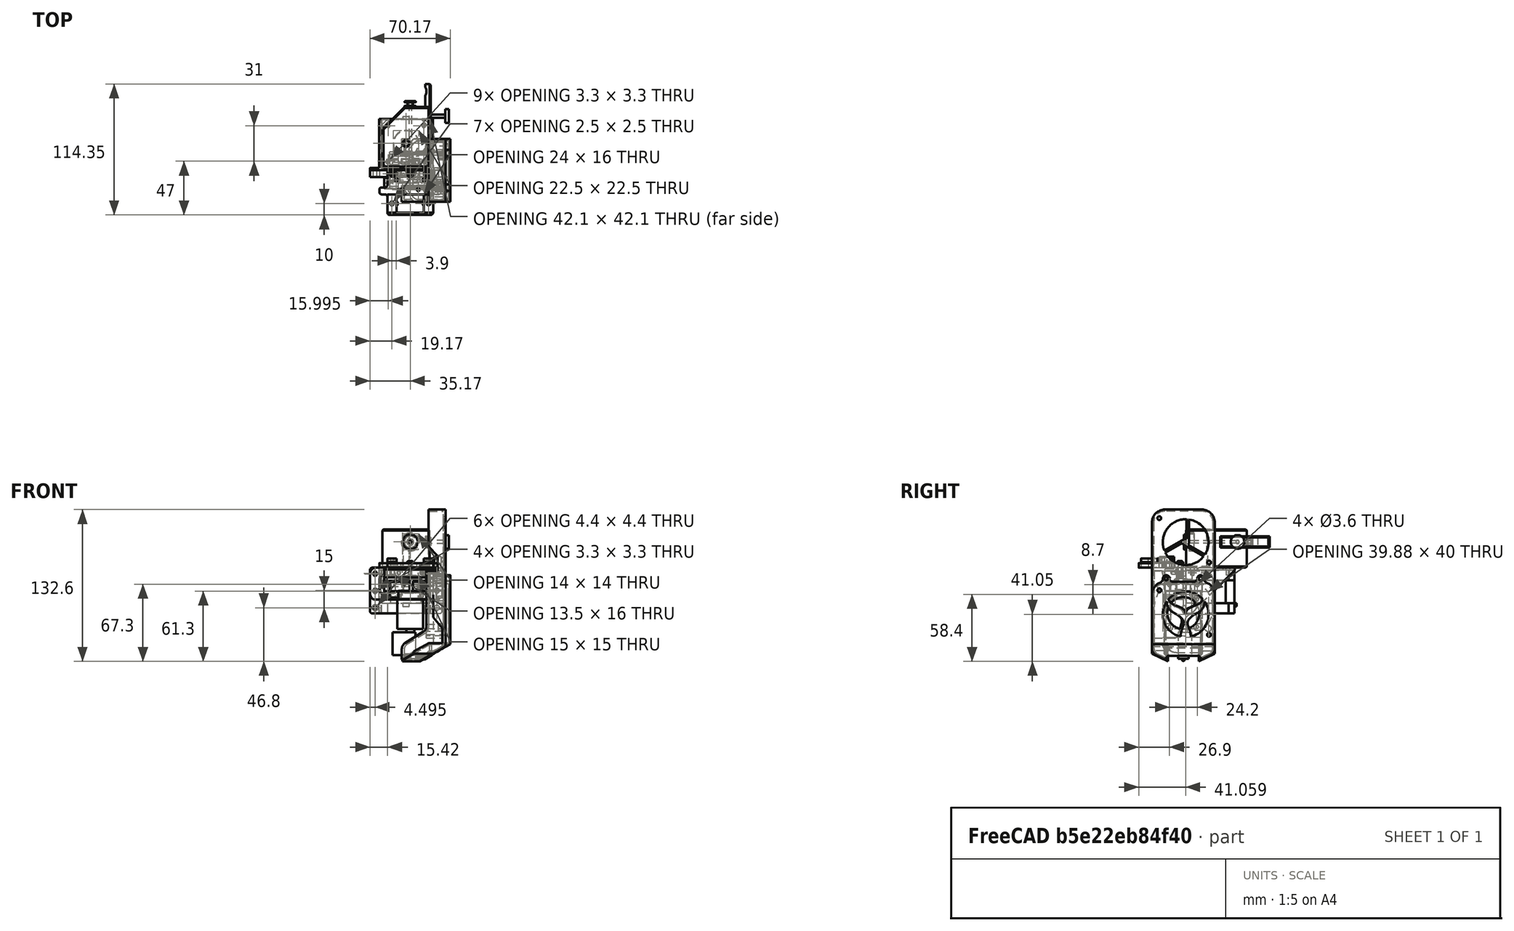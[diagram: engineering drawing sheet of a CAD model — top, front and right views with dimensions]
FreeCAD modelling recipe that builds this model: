
FCSTD DOCUMENT  (FreeCAD 0.21R33675 (Git))
Label: V6火山+5015方案B
License: All rights reserved
LicenseURL: http://en.wikipedia.org/wiki/All_rights_reserved
objects: Sketcher::SketchObject×31, PartDesign::Pad×16, PartDesign::Pocket×15, Part::Feature×13, PartDesign::Body×6, PartDesign::Fillet×4, PartDesign::Chamfer×4, PartDesign::Thickness×2, Part::Fuse×2, PartDesign::Revolution×1, App::Part×1, PartDesign::Mirrored×1, Part::Mirroring×1
note: 138 computed .brp shape members not serialized (recipe doc carries the construction recipe); baked Part::Feature solids carry a one-line shape summary decoded from their .brp

FEATURE [Sketcher::SketchObject] Sketch015
  FullyConstrained = true
  MapMode = 5
  Placement = pos=(0,0,0) rot=(0.57735,0.57735,0.57735;2.0944rad)
  Support = -> [YZ_Plane002]
  sketch-geometry (17):
    g0: LineSegment StartX=0 StartY=4 StartZ=0 EndX=8 EndY=4 EndZ=0
    g1: LineSegment StartX=8 StartY=4 StartZ=0 EndX=8 EndY=0 EndZ=0
    g2: LineSegment StartX=8 StartY=0 StartZ=0 EndX=6 EndY=0 EndZ=0
    g3: LineSegment StartX=6 StartY=0 StartZ=0 EndX=6 EndY=-6 EndZ=0
    g4: LineSegment StartX=6 StartY=-6 StartZ=0 EndX=8 EndY=-6 EndZ=0
    g5: LineSegment StartX=8 StartY=-6 StartZ=0 EndX=8 EndY=-12.5 EndZ=0
    g6: LineSegment StartX=8 StartY=-12.5 StartZ=0 EndX=11.15 EndY=-12.5 EndZ=0
    g7: LineSegment StartX=11.15 StartY=-12.5 StartZ=0 EndX=11.15 EndY=-39 EndZ=0
    g8: LineSegment StartX=11.15 StartY=-39 StartZ=0 EndX=3.5 EndY=-39 EndZ=0
    g9: LineSegment StartX=0.5 StartY=-67 StartZ=0 EndX=0 EndY=-67 EndZ=0
    g10: LineSegment StartX=3.5 StartY=-39 StartZ=0 EndX=3.5 EndY=-62 EndZ=0
    g11: LineSegment StartX=0 StartY=4 StartZ=0 EndX=0 EndY=-67 EndZ=0
    g12: GeomPoint X=3.5 Y=-42 Z=0
    g13: LineSegment StartX=3.5 StartY=-62 StartZ=0 EndX=4.5 EndY=-62 EndZ=0
    g14: LineSegment StartX=4.5 StartY=-62 StartZ=0 EndX=4.5 EndY=-65 EndZ=0
    g15: LineSegment StartX=4.5 StartY=-65 StartZ=0 EndX=1.90042 EndY=-65 EndZ=0
    g16: LineSegment StartX=1.90042 StartY=-65 StartZ=0 EndX=0.5 EndY=-67 EndZ=0
  constraints (50):
    c: PointOnObject(g0,g-2)
    c: Horizontal(g0)
    c: Coincident(g1,g0)
    c: Vertical(g1)
    c: Coincident(g2,g1)
    c: Coincident(g3,g2)
    c: Coincident(g4,g3)
    c: Horizontal(g4)
    c: Horizontal(g2)
    c: Distance(g0) = 8
    c: Distance(g1) = 4
    c: Distance(g3) = 6
    c: Distance(g2) = 2
    c: Distance(g4) = 2
    c: Coincident(g5,g4)
    c: Horizontal(g6)
    c: Coincident(g7,g6)
    c: Vertical(g7)
    c: Vertical(g5)
    c: Coincident(g6,g5)
    c: DistanceX(g-2,g6) = 11.15
    c: Coincident(g8,g7)
    c: Horizontal(g8)
    c: DistanceX(g-2,g8) = 3.5
    c: DistanceY(g7,g0) = 43
    c: Distance(g5) = 6.5
    c: PointOnObject(g9,g-2)
    c: Horizontal(g9)
    c: Distance(g9) = 0.5
    c: Coincident(g10,g8)
    c: Vertical(g10)
    c: Coincident(g11,g0)
    c: Coincident(g11,g9)
    c: Vertical(g3)
    c: PointOnObject(g2,g-1)
    c: PointOnObject(g12,g10)
    c: Distance(g12,g8) = 3
    c: Distance(g12,g10) = 20
    c: Coincident(g10,g13)
    c: Horizontal(g13)
    c: Coincident(g13,g14)
    c: Vertical(g14)
    c: Coincident(g14,g15)
    c: Horizontal(g15)
    c: Coincident(g15,g16)
    c: Coincident(g16,g9)
    c: Angle(g16,g15) = 2.18166
    c: Distance(g13) = 1
    c: DistanceY(g9,g13) = 5
    c: Distance(g14) = 3
FEATURE [PartDesign::Revolution] Revolution
  Angle = 360
  Axis = (-2e-16,3e-16,1)
  Base = (0,0,0)
  Placement = pos=(0,0,0) rot=(0.57735,0.57735,0.57735;2.0944rad)
  Profile = -> Sketch015
  ReferenceAxis = -> Sketch015 [V_Axis]
  Reversed = true
FEATURE [Sketcher::SketchObject] Sketch016
  ExternalGeometry = -> [Revolution]
  FullyConstrained = true
  MapMode = 5
  Placement = pos=(0,0,0) rot=(1,0,0;1.5708rad)
  Support = -> [XZ_Plane002]
  sketch-geometry (6):
    g0: LineSegment StartX=-3.5 StartY=-62 StartZ=0 EndX=-15.5 EndY=-62 EndZ=0
    g1: LineSegment StartX=-15.5 StartY=-62 StartZ=0 EndX=-15.5 EndY=-42 EndZ=0
    g2: LineSegment StartX=-15.5 StartY=-42 StartZ=0 EndX=4.5 EndY=-42 EndZ=0
    g3: LineSegment StartX=4.5 StartY=-42 StartZ=0 EndX=4.5 EndY=-62 EndZ=0
    g4: LineSegment StartX=4.5 StartY=-62 StartZ=0 EndX=3.5 EndY=-62 EndZ=0
    g5: LineSegment StartX=-3.5 StartY=-62 StartZ=0 EndX=3.5 EndY=-62 EndZ=0
  constraints (16):
    c: Coincident(g0,g-3)
    c: Horizontal(g0)
    c: Coincident(g1,g0)
    c: Vertical(g1)
    c: Coincident(g2,g1)
    c: Horizontal(g2)
    c: Coincident(g3,g2)
    c: Vertical(g3)
    c: Coincident(g4,g3)
    c: Coincident(g4,g-3)
    c: Horizontal(g4)
    c: Distance(g3) = 20
    c: Distance(g1,g2) = 20
    c: DistanceX(g-2,g0) = -15.5
    c: Coincident(g5,g0)
    c: Coincident(g5,g4)
FEATURE [PartDesign::Pad] Pad006  label="薄"
  BaseFeature = -> Revolution
  Direction = (0,-1,-2e-16)
  Length = 4.5
  Length2 = 10
  Placement = pos=(0,0,0) rot=(0.57735,0.57735,0.57735;2.0944rad)
  Profile = -> Sketch016
  ReferenceAxis = -> Sketch016 [N_Axis]
  Type = 0
FEATURE [PartDesign::Pad] Pad007  label="厚"
  BaseFeature = -> Pad006
  Direction = (0,-1,-2e-16)
  Length = 7
  Length2 = 10
  Placement = pos=(0,0,0) rot=(0.57735,0.57735,0.57735;2.0944rad)
  Profile = -> Sketch016
  ReferenceAxis = -> Sketch016 [N_Axis]
  Reversed = true
  Type = 0
FEATURE [PartDesign::Body] Body002  label="E3DV6火山（玻璃热敏）"
  Group = -> [Sketch015,Revolution,Sketch016,Pad006,Pad007]
  Origin = -> Origin002
  Tip = -> Pad007
FEATURE [Part::Feature] Part__Feature166  label="<unrecoverable-encoding: 13 bytes cea2d18dd09ecebbbfaab9d6... md5=9adbc4b6>A125V003"
  Placement = pos=(23.9,-14.5,21.31) rot=(0,0,-1;1.5708rad)
  shape: bbox 13.5 x 14.59 x 5.62 mm, 42 faces (baked)
FEATURE [Part::Feature] Part__Feature167  label="MGN12H»¬¿002"
  Placement = pos=(0,-19,0) rot=(0,-1,0;1.5708rad)
  shape: bbox 45.4 x 10 x 27 mm, 34 faces (baked)
FEATURE [Part::Feature] Part__Feature169  label="ɢɈ¹ܰ²װ°"
  Placement = pos=(0,-19.5,16.5) rot=(0,0,1;0rad)
  shape: bbox 54 x 39 x 4 mm, 68 faces (baked)
FEATURE [Part::Feature] Part__Feature172  label="同步带压片"
  Placement = pos=(-16,-29,21) rot=(0,0,1;0rad)
  shape: bbox 8 x 16 x 3 mm, 12 faces (baked)
FEATURE [Part::Feature] Part__Feature173  label="同步带压片001"
  Placement = pos=(16,-29,21) rot=(0,1,0;3.14159rad)
  shape: bbox 8 x 16 x 3 mm, 12 faces (baked)
FEATURE [Part::Feature] Part__Feature174  label="42步进电机004"
  Placement = pos=(-3.675,23.5,12.5) rot=(0,0,1;0rad)
  shape: bbox 42.3 x 44.3 x 62 mm, 50 faces (baked)
FEATURE [Part::Feature] Part__Feature175  label="42步进电机支架"
  Placement = pos=(-3.675,23.5,14.5) rot=(0,0,1;0rad)
  shape: bbox 63 x 45 x 40 mm, 42 faces (baked)
FEATURE [Part::Feature] Part__Feature176  label="MGN12H滑筷棯接颁灅住"
  Placement = pos=(0,0,0) rot=(0.57735,-0.57735,-0.57735;2.0944rad)
  shape: bbox 63 x 6 x 28 mm, 64 faces (baked)
FEATURE [Part::Feature] Part__Feature177  label="BMG挤出机"
  Placement = pos=(0,2.35,37) rot=(0,0,1;0rad)
  shape: bbox 58 x 75 x 33.5 mm, 84 faces (baked)
FEATURE [Part::Feature] Part__Feature179  label="内六角平圆头螺钉M3¡Á029"
  Placement = pos=(0,-3,18.5) rot=(1,0,0;1.5708rad)
  shape: bbox 6.17 x 6.17 x 12.2 mm, 24 faces (baked)
FEATURE [Part::Feature] Part__Feature180  label="内六角平圆头螺钉M3¡Á030"
  Placement = pos=(15,-3,18.5) rot=(1,0,0;1.5708rad)
  shape: bbox 6.17 x 6.17 x 12.2 mm, 24 faces (baked)
FEATURE [Part::Feature] Part__Feature178  label="内六角平圆头螺钉M3¡Á028"
  Placement = pos=(-15,-3,18.5) rot=(1,0,0;1.5708rad)
  shape: bbox 6.17 x 6.17 x 12.2 mm, 24 faces (baked)
FEATURE [App::Part] CR10________________________1  label="CR10近程喷嘴模块1"
  Group = -> [Part__Feature166,Part__Feature167,Part__Feature169,Part__Feature172,Part__Feature173,Part__Feature174,Part__Feature175,Part__Feature176,Part__Feature177,Part__Feature178,Part__Feature179,Part__Feature180]
  Origin = -> Origin006
  Placement = pos=(-36.5,0,8.1) rot=(0.57735,0.57735,0.57735;2.0944rad)
FEATURE [Sketcher::SketchObject] Sketch017
  FullyConstrained = true
  MapMode = 5
  Placement = pos=(0,0,0) rot=(0.57735,0.57735,0.57735;2.0944rad)
  Support = -> [YZ_Plane007]
  sketch-geometry (18):
    g0: LineSegment StartX=-16 StartY=2.25 StartZ=0 EndX=-16 EndY=0 EndZ=0
    g1: LineSegment StartX=-16 StartY=0 StartZ=0 EndX=-16 EndY=-5.8 EndZ=0
    g2: LineSegment StartX=-16 StartY=-5.8 StartZ=0 EndX=-16 EndY=-11.8 EndZ=0
    g3: LineSegment StartX=-16 StartY=-11.8 StartZ=0 EndX=16 EndY=-11.8 EndZ=0
    g4: LineSegment StartX=16 StartY=-11.8 StartZ=0 EndX=16 EndY=-5.8 EndZ=0
    g5: LineSegment StartX=16 StartY=-5.8 StartZ=0 EndX=16 EndY=0 EndZ=0
    g6: LineSegment StartX=16 StartY=0 StartZ=0 EndX=16 EndY=2.25 EndZ=0
    g7: Circle CenterX=-7 CenterY=-8.9 CenterZ=0 NormalX=0 NormalY=0 NormalZ=1 AngleXU=0 Radius=1.8
    g8: Circle CenterX=7 CenterY=-8.9 CenterZ=0 NormalX=0 NormalY=0 NormalZ=1 AngleXU=0 Radius=1.8
    g9: Circle CenterX=-12.1 CenterY=-0.2 CenterZ=0 NormalX=0 NormalY=0 NormalZ=1 AngleXU=0 Radius=1.8
    g10: Circle CenterX=12.1 CenterY=-0.2 CenterZ=0 NormalX=0 NormalY=0 NormalZ=1 AngleXU=0 Radius=1.8
    g11: ArcOfCircle CenterX=-12.1 CenterY=-0.2 CenterZ=0 NormalX=0 NormalY=0 NormalZ=1 AngleXU=0 Radius=3.15 StartAngle=0.891123 EndAngle=2.25047
    g12: ArcOfCircle CenterX=12.1 CenterY=-0.2 CenterZ=0 NormalX=0 NormalY=0 NormalZ=1 AngleXU=0 Radius=3.15 StartAngle=0.891123 EndAngle=2.25047
    g13: LineSegment StartX=-14.0799 StartY=2.25 StartZ=0 EndX=-16 EndY=2.25 EndZ=0
    g14: LineSegment StartX=10.1201 StartY=2.25 StartZ=0 EndX=-10.1201 EndY=2.25 EndZ=0
    g15: LineSegment StartX=14.0799 StartY=2.25 StartZ=0 EndX=16 EndY=2.25 EndZ=0
    g16: LineSegment StartX=10.1201 StartY=2.25 StartZ=0 EndX=14.0799 EndY=2.25 EndZ=0
    g17: LineSegment StartX=-14.0799 StartY=2.25 StartZ=0 EndX=-10.1201 EndY=2.25 EndZ=0
  constraints (49):
    c: Vertical(g0)
    c: Coincident(g0,g1)
    c: Vertical(g1)
    c: Coincident(g1,g2)
    c: Vertical(g2)
    c: Coincident(g2,g3)
    c: Coincident(g3,g4)
    c: Vertical(g4)
    c: Coincident(g4,g5)
    c: Vertical(g5)
    c: Coincident(g5,g6)
    c: Vertical(g6)
    c: Coincident(g13,g0)
    c: Equal(g2,g4)
    c: Equal(g5,g1)
    c: Symmetric(g3,g2,g-2)
    c: PointOnObject(g5,g-1)
    c: Distance(g5) = 5.8
    c: Distance(g4) = 6
    c: Equal(g8,g7)
    c: Symmetric(g8,g7,g-2)
    c: Distance(g7,g8) = 14
    c: Diameter(g8) = 3.6
    c: Distance(g8,g3) = 2.9
    c: Symmetric(g10,g9,g-2)
    c: Equal(g10,g9)
    c: Distance(g10,g9) = 24.2
    c: Diameter(g10) = 3.6
    c: DistanceY(g8,g10) = 8.7
    c: Distance(g0) = 2.25
    c: Coincident(g11,g9)
    c: Coincident(g12,g10)
    c: Equal(g12,g11)
    c: Diameter(g12) = 6.3
    c: Coincident(g14,g11)
    c: Coincident(g14,g12)
    c: Distance(g0,g6) = 32
    c: Equal(g6,g0)
    c: Coincident(g15,g12)
    c: Coincident(g15,g6)
    c: Horizontal(g15)
    c: Horizontal(g13)
    c: Coincident(g16,g12)
    c: Coincident(g16,g12)
    c: Horizontal(g16)
    c: Coincident(g17,g11)
    c: Coincident(g17,g11)
    c: Horizontal(g17)
    c: Coincident(g11,g13)
FEATURE [PartDesign::Pad] Pad008
  Direction = (1,-2e-16,3e-16)
  Length = 18
  Length2 = 10
  Placement = pos=(0,0,0) rot=(0.57735,0.57735,0.57735;2.0944rad)
  Profile = -> Sketch017
  ReferenceAxis = -> Sketch017 [N_Axis]
  Reversed = true
  Type = 0
FEATURE [Sketcher::SketchObject] Sketch018
  ExternalGeometry = -> [Pad008]
  FullyConstrained = true
  MapMode = 5
  Placement = pos=(0,0,0) rot=(0.57735,0.57735,0.57735;2.0944rad)
  Support = -> [Pad008]
  sketch-geometry (4):
    g0: LineSegment StartX=-16 StartY=-5.8 StartZ=0 EndX=16 EndY=-5.8 EndZ=0
    g1: LineSegment StartX=16 StartY=-5.8 StartZ=0 EndX=16 EndY=-11.8 EndZ=0
    g2: LineSegment StartX=16 StartY=-11.8 StartZ=0 EndX=-16 EndY=-11.8 EndZ=0
    g3: LineSegment StartX=-16 StartY=-11.8 StartZ=0 EndX=-16 EndY=-5.8 EndZ=0
  constraints (11):
    c: Coincident(g0,g1)
    c: Coincident(g1,g2)
    c: Coincident(g2,g3)
    c: Coincident(g3,g0)
    c: Horizontal(g0)
    c: Horizontal(g2)
    c: Vertical(g1)
    c: Vertical(g3)
    c: Coincident(g-3,g1)
    c: Equal(g2,g-3)
    c: Distance(g1) = 6
FEATURE [PartDesign::Pocket] Pocket
  BaseFeature = -> Pad008
  Direction = (-1,4e-16,-4e-16)
  Length = 10.5
  Length2 = 5
  Placement = pos=(0,0,0) rot=(0.57735,0.57735,0.57735;2.0944rad)
  Profile = -> Sketch018
  ReferenceAxis = -> Sketch018 [N_Axis]
  Type = 0
FEATURE [Sketcher::SketchObject] Sketch019
  ExternalGeometry = -> [Pocket]
  FullyConstrained = true
  MapMode = 5
  Placement = pos=(-6e-16,1e-15,2.25) rot=(0,0,-1;1.5708rad)
  Support = -> [Pocket]
  sketch-geometry (2):
    g0: ArcOfCircle CenterX=0 CenterY=2e-15 CenterZ=0 NormalX=0 NormalY=0 NormalZ=1 AngleXU=0 Radius=6.2 StartAngle=3.14159 EndAngle=6.28319
    g1: LineSegment StartX=-6.2 StartY=2.8e-15 StartZ=0 EndX=6.2 EndY=5e-16 EndZ=0
  constraints (7):
    c: PointOnObject(g0,g-2)
    c: PointOnObject(g0,g-3)
    c: PointOnObject(g0,g-3)
    c: PointOnObject(g0,g-3)
    c: Coincident(g1,g0)
    c: Coincident(g1,g0)
    c: Diameter(g0) = 12.4
FEATURE [PartDesign::Pocket] Pocket001
  BaseFeature = -> Pocket
  Direction = (7e-16,-7e-16,-1)
  Length = 5
  Length2 = 5
  Placement = pos=(0,0,0) rot=(0.57735,0.57735,0.57735;2.0944rad)
  Profile = -> Sketch019
  ReferenceAxis = -> Sketch019 [N_Axis]
  Type = 1
FEATURE [Sketcher::SketchObject] Sketch020
  ExternalGeometry = -> [Pocket001]
  FullyConstrained = true
  MapMode = 5
  Placement = pos=(-6e-16,1e-15,2.25) rot=(0,0,-1;1.5708rad)
  Support = -> [Pocket001]
  sketch-geometry (3):
    g0: LineSegment StartX=-6.2 StartY=2.4e-15 StartZ=0 EndX=6.2 EndY=-1.1e-15 EndZ=0
    g1: ArcOfCircle CenterX=0 CenterY=6e-16 CenterZ=0 NormalX=0 NormalY=0 NormalZ=1 AngleXU=0 Radius=8.2 StartAngle=3.14159 EndAngle=6.28319
    g2: LineSegment StartX=-8.2 StartY=2.9e-15 StartZ=0 EndX=8.2 EndY=-1.4e-15 EndZ=0
  constraints (9):
    c: Coincident(g0,g-4)
    c: Coincident(g0,g-3)
    c: PointOnObject(g1,g-2)
    c: PointOnObject(g1,g-3)
    c: PointOnObject(g1,g-4)
    c: PointOnObject(g1,g0)
    c: Diameter(g1) = 16.4
    c: Coincident(g2,g1)
    c: Coincident(g2,g1)
FEATURE [PartDesign::Pocket] Pocket002
  BaseFeature = -> Pocket001
  Direction = (1.1e-15,-8e-16,-1)
  Length = 2.25
  Length2 = 5
  Placement = pos=(0,0,0) rot=(0.57735,0.57735,0.57735;2.0944rad)
  Profile = -> Sketch020
  ReferenceAxis = -> Sketch020 [N_Axis]
  Type = 0
FEATURE [Sketcher::SketchObject] Sketch
  FullyConstrained = true
  MapMode = 5
  Placement = pos=(0,0,0) rot=(0.57735,0.57735,0.57735;2.0944rad)
  Support = -> [Pocket002]
  sketch-geometry (4):
    g0: LineSegment StartX=-19.6231 StartY=8.25432 StartZ=0 EndX=19.6394 EndY=8.25432 EndZ=0
    g1: LineSegment StartX=19.6394 StartY=8.25432 StartZ=0 EndX=19.6394 EndY=-15.6805 EndZ=0
    g2: LineSegment StartX=19.6394 StartY=-15.6805 StartZ=0 EndX=-19.6231 EndY=-15.6805 EndZ=0
    g3: LineSegment StartX=-19.6231 StartY=-15.6805 StartZ=0 EndX=-19.6231 EndY=8.25432 EndZ=0
  constraints (12):
    c: Coincident(g0,g1)
    c: Coincident(g1,g2)
    c: Coincident(g2,g3)
    c: Coincident(g3,g0)
    c: Horizontal(g0)
    c: Horizontal(g2)
    c: Vertical(g1)
    c: Vertical(g3)
    c: DistanceX(g0) = -19.6231
    c: DistanceY(g0) = 8.25432
    c: DistanceX(g1) = 19.6394
    c: DistanceY(g1) = -15.6805
FEATURE [PartDesign::Pocket] Pocket003
  BaseFeature = -> Pocket002
  Direction = (-1,1.1e-15,-7e-16)
  Length = 0.5
  Length2 = 5
  Placement = pos=(0,0,0) rot=(0.57735,0.57735,0.57735;2.0944rad)
  Profile = -> Sketch
  ReferenceAxis = -> Sketch [N_Axis]
  Type = 0
FEATURE [PartDesign::Body] Body003  label="贴墙端"
  Group = -> [Sketch017,Pad008,Sketch018,Pocket,Sketch019,Pocket001,Sketch020,Pocket002,Sketch,Pocket003]
  Origin = -> Origin007
  Tip = -> Pocket003
FEATURE [Part::Feature] Part__Feature  label="5015µ¼·耚"
  Placement = pos=(22.5,0,-13.2) rot=(0.57735,0.57735,0.57735;2.0944rad)
  shape: bbox 38.35 x 55 x 131 mm, 194 faces (baked)
FEATURE [Sketcher::SketchObject] Sketch021
  FullyConstrained = false
  MapMode = 5
  Placement = pos=(0,0,0) rot=(0.57735,0.57735,0.57735;2.0944rad)
  Support = -> [YZ_Plane]
  sketch-geometry (17):
    g0: LineSegment StartX=-25.8 StartY=-46.9 StartZ=0 EndX=-5.8 EndY=-46.9 EndZ=0
    g1: LineSegment StartX=-5.8 StartY=-46.9 StartZ=0 EndX=-5.8 EndY=-43.8256 EndZ=0
    g2: LineSegment StartX=-25.8 StartY=-46.9 StartZ=0 EndX=-25.8 EndY=-21.5 EndZ=0
    g3: ArcOfCircle CenterX=1.9 CenterY=-21.2 CenterZ=0 NormalX=0 NormalY=0 NormalZ=1 AngleXU=0 Radius=23.9 StartAngle=4.38436 EndAngle=5.45674
    g4: ArcOfCircle CenterX=1.9 CenterY=-21.2 CenterZ=0 NormalX=0 NormalY=0 NormalZ=1 AngleXU=0 Radius=23.9 StartAngle=5.66632 EndAngle=6.28319
    g5: LineSegment StartX=21.3952 StartY=-35.0256 StartZ=0 EndX=23.5516 EndY=-36.9232 EndZ=0
    g6: LineSegment StartX=18.0921 StartY=-38.7792 StartZ=0 EndX=20.2484 EndY=-40.6768 EndZ=0
    g7: LineSegment StartX=-20.3952 StartY=-4.87439 StartZ=0 EndX=-22.5516 EndY=-2.97678 EndZ=0
    g8: ArcOfCircle CenterX=-20.9 CenterY=-1.1 CenterZ=0 NormalX=0 NormalY=0 NormalZ=1 AngleXU=0 Radius=2.5 StartAngle=0.849141 EndAngle=3.99073
    g9: ArcOfCircle CenterX=21.9 CenterY=-38.8 CenterZ=0 NormalX=0 NormalY=0 NormalZ=1 AngleXU=0 Radius=2.5 StartAngle=3.99073 EndAngle=7.13233
    g10: LineSegment StartX=-19.2484 StartY=0.776784 StartZ=0 EndX=-17.0921 EndY=-1.12083 EndZ=0
    g11: ArcOfCircle CenterX=0.0547185 CenterY=-21.0457 CenterZ=0 NormalX=0 NormalY=0 NormalZ=1 AngleXU=0 Radius=25.7457 StartAngle=6.27719 EndAngle=7.85611
    g12: ArcOfCircle CenterX=-1.06983 CenterY=-20.1632 CenterZ=0 NormalX=0 NormalY=0 NormalZ=1 AngleXU=0 Radius=24.8862 StartAngle=1.52779 EndAngle=2.27027
    g13: ArcOfCircle CenterX=7.23359 CenterY=-23.0475 CenterZ=0 NormalX=0 NormalY=0 NormalZ=1 AngleXU=0 Radius=33.0698 StartAngle=2.55978 EndAngle=3.09478
    g14: GeomPoint X=21.9 Y=-41.3 Z=0
    g15: LineSegment StartX=25.8 StartY=-21.2 StartZ=0 EndX=0 EndY=-21.2 EndZ=0
    g16: LineSegment StartX=-25.8 StartY=-21.5 StartZ=0 EndX=0 EndY=-21.5 EndZ=0
  constraints (49):
    c: Coincident(g0,g1)
    c: Vertical(g1)
    c: Coincident(g0,g2)
    c: Distance(g0) = 20
    c: Coincident(g4,g3)
    c: Distance(g2) = 25.4
    c: Coincident(g4,g5)
    c: Coincident(g3,g6)
    c: Parallel(g6,g5)
    c: Coincident(g1,g3)
    c: Horizontal(g0)
    c: Vertical(g2)
    c: DistanceY(g3) = -21.2
    c: Tangent(g9,g5) = 1.5708
    c: Tangent(g8,g7) = 1.5708
    c: Tangent(g9,g6) = -1.5708
    c: DistanceX(g8,g3) = 22.8
    c: Equal(g5,g6)
    c: DistanceX(g0,g3) = 27.7
    c: DistanceX(g3,g9) = 20
    c: DistanceY(g3,g8) = 20.1
    c: Equal(g9,g8)
    c: Parallel(g7,g10)
    c: Equal(g10,g7)
    c: Tangent(g10,g8) = 1.5708
    c: Equal(g3,g4)
    c: Coincident(g11,g4)
    c: Coincident(g12,g11)
    c: Coincident(g12,g10)
    c: DistanceY(g0,g11) = 51.6
    c: PointOnObject(g11,g-2)
    c: Horizontal(g4,g3)
    c: DistanceX(g0,g4) = 51.6
    c: DistanceY(g9,g4) = 17.6
    c: Parallel(g7,g6)
    c: Coincident(g13,g7)
    c: Coincident(g13,g2)
    c: Diameter(g9) = 5
    c: Equal(g6,g7)
    c: PointOnObject(g14,g9)
    c: Vertical(g14,g9)
    c: DistanceY(g0,g14) = 5.6
    c: Coincident(g15,g4)
    c: PointOnObject(g15,g-2)
    c: Horizontal(g15)
    c: Coincident(g16,g2)
    c: PointOnObject(g16,g-2)
    c: Horizontal(g16)
    c: Equal(g15,g16)
FEATURE [PartDesign::Pad] Pad
  Direction = (1,-2e-16,3e-16)
  Length = 15
  Length2 = 10
  Placement = pos=(0,0,0) rot=(0.57735,0.57735,0.57735;2.0944rad)
  Profile = -> Sketch021
  ReferenceAxis = -> Sketch021 [N_Axis]
  Type = 0
FEATURE [PartDesign::Body] Body  label="5015风扇"
  Group = -> [Sketch021,Pad]
  Origin = -> Origin
  Placement = pos=(14,0,0) rot=(0,0,1;0rad)
  Tip = -> Pad
FEATURE [Sketcher::SketchObject] Sketch116
  FullyConstrained = true
  MapMode = 5
  Placement = pos=(0,0,0) rot=(0.57735,0.57735,0.57735;2.0944rad)
  Support = -> [YZ_Plane020]
  sketch-geometry (14):
    g0: Circle CenterX=15 CenterY=56.45 CenterZ=0 NormalX=0 NormalY=0 NormalZ=1 AngleXU=0 Radius=1.65
    g1: Circle CenterX=-15 CenterY=56.45 CenterZ=0 NormalX=0 NormalY=0 NormalZ=1 AngleXU=0 Radius=1.65
    g2: LineSegment StartX=27.5 StartY=42.0963 StartZ=0 EndX=27.5 EndY=0 EndZ=0
    g3: LineSegment StartX=27.5 StartY=0 StartZ=0 EndX=-27.5 EndY=0 EndZ=0
    g4: LineSegment StartX=-27.5 StartY=0 StartZ=0 EndX=-27.5 EndY=42.0963 EndZ=0
    g5: ArcOfCircle CenterX=-16 CenterY=42.0963 CenterZ=0 NormalX=0 NormalY=0 NormalZ=1 AngleXU=0 Radius=11.5 StartAngle=1.9578 EndAngle=3.14159
    g6: ArcOfCircle CenterX=16 CenterY=42.0963 CenterZ=0 NormalX=0 NormalY=0 NormalZ=1 AngleXU=0 Radius=11.5 StartAngle=4e-16 EndAngle=1.18379
    g7: ArcOfCircle CenterX=-15 CenterY=56.45 CenterZ=0 NormalX=0 NormalY=0 NormalZ=1 AngleXU=0 Radius=2.85 StartAngle=1.1e-15 EndAngle=3.14159
    g8: ArcOfCircle CenterX=15 CenterY=56.45 CenterZ=0 NormalX=0 NormalY=0 NormalZ=1 AngleXU=0 Radius=2.85 StartAngle=0 EndAngle=3.14159
    g9: ArcOfCircle CenterX=9.3 CenterY=56.45 CenterZ=0 NormalX=0 NormalY=0 NormalZ=1 AngleXU=0 Radius=2.85 StartAngle=4.71239 EndAngle=6.28319
    g10: ArcOfCircle CenterX=21.85 CenterY=56.45 CenterZ=0 NormalX=0 NormalY=0 NormalZ=1 AngleXU=0 Radius=4 StartAngle=3.14159 EndAngle=4.32538
    g11: ArcOfCircle CenterX=-9.3 CenterY=56.45 CenterZ=0 NormalX=0 NormalY=0 NormalZ=1 AngleXU=0 Radius=2.85 StartAngle=3.14159 EndAngle=4.71239
    g12: ArcOfCircle CenterX=-21.85 CenterY=56.45 CenterZ=0 NormalX=0 NormalY=0 NormalZ=1 AngleXU=0 Radius=4 StartAngle=5.0994 EndAngle=6.28319
    g13: LineSegment StartX=-9.3 StartY=53.6 StartZ=0 EndX=9.3 EndY=53.6 EndZ=0
  constraints (36):
    c: Symmetric(g1,g0,g-2)
    c: Diameter(g0) = 3.3
    c: DistanceX(g0) = 15
    c: Equal(g1,g0)
    c: Coincident(g3,g4)
    c: Vertical(g2)
    c: Vertical(g4)
    c: Coincident(g2,g3)
    c: Equal(g6,g5)
    c: Tangent(g6,g2) = 1.5708
    c: Tangent(g5,g4) = 1.5708
    c: Symmetric(g2,g3,g-2)
    c: Distance(g3) = 55
    c: Radius(g6) = 11.5
    c: Coincident(g7,g1)
    c: Coincident(g8,g0)
    c: Equal(g8,g7)
    c: Horizontal(g9,g8)
    c: Horizontal(g11,g7)
    c: Horizontal(g12,g7)
    c: Tangent(g13,g11) = -1.5708
    c: Tangent(g5,g12) = 1.5708
    c: Tangent(g6,g10) = 1.5708
    c: Diameter(g10) = 8
    c: Diameter(g9) = 5.7
    c: Tangent(g9,g13) = -1.5708
    c: Tangent(g8,g9) = 1.5708
    c: Tangent(g8,g10) = 1.5708
    c: Diameter(g11) = 5.7
    c: Equal(g12,g10)
    c: Tangent(g7,g12) = 1.5708
    c: Tangent(g7,g11) = 1.5708
    c: Diameter(g8) = 5.7
    c: Horizontal(g8,g8)
    c: DistanceY(g2,g9) = 53.6
    c: PointOnObject(g-1,g3)
FEATURE [PartDesign::Pad] Pad043
  Direction = (1,-2e-16,3e-16)
  Length = 15
  Length2 = 10
  Placement = pos=(0,0,0) rot=(0.57735,0.57735,0.57735;2.0944rad)
  Profile = -> Sketch116
  ReferenceAxis = -> Sketch116 [N_Axis]
  Reversed = true
  Type = 0
FEATURE [Sketcher::SketchObject] Sketch117
  AttachmentOffset = pos=(0,0,0) rot=(0,0,1;3.14159rad)
  ExternalGeometry = -> [Pad043]
  FullyConstrained = true
  MapMode = 5
  Placement = pos=(-15,3.3e-15,-3.3e-15) rot=(0.57735,-0.57735,-0.57735;2.0944rad)
  Support = -> [Pad043]
  sketch-geometry (9):
    g0: LineSegment StartX=-25.9 StartY=42.0963 StartZ=0 EndX=-25.9 EndY=1.42e-14 EndZ=0
    g1: LineSegment StartX=-25.9 StartY=1.5e-14 StartZ=0 EndX=25.9 EndY=1.5e-14 EndZ=0
    g2: LineSegment StartX=25.9 StartY=1.5e-14 StartZ=0 EndX=25.9 EndY=42.0963 EndZ=0
    g3: LineSegment StartX=-15.9963 StartY=52 StartZ=0 EndX=15.9963 EndY=52 EndZ=0
    g4: ArcOfCircle CenterX=-15.9963 CenterY=42.0963 CenterZ=0 NormalX=0 NormalY=0 NormalZ=1 AngleXU=0 Radius=9.90366 StartAngle=1.5708 EndAngle=3.14159
    g5: ArcOfCircle CenterX=15.9963 CenterY=42.0963 CenterZ=0 NormalX=0 NormalY=0 NormalZ=1 AngleXU=0 Radius=9.90366 StartAngle=1e-16 EndAngle=1.5708
    g6: LineSegment StartX=9.3 StartY=53.6 StartZ=0 EndX=9.3 EndY=52 EndZ=0
    g7: LineSegment StartX=25.9 StartY=1.5e-14 StartZ=0 EndX=27.5 EndY=1.6e-14 EndZ=0
    g8: LineSegment StartX=-25.9 StartY=1.5e-14 StartZ=0 EndX=-27.5 EndY=-1.76e-14 EndZ=0
  constraints (23):
    c: Vertical(g0)
    c: Coincident(g0,g1)
    c: Horizontal(g1)
    c: Coincident(g1,g2)
    c: Vertical(g2)
    c: Tangent(g5,g3) = 1.5708
    c: Tangent(g5,g2) = -1.5708
    c: Tangent(g4,g3) = 1.5708
    c: Tangent(g4,g0) = -1.5708
    c: PointOnObject(g1,g-8)
    c: DistanceY(g3,g-5) = 1.6
    c: Horizontal(g3)
    c: Coincident(g6,g-5)
    c: PointOnObject(g6,g3)
    c: Coincident(g7,g1)
    c: Coincident(g7,g-8)
    c: Coincident(g8,g0)
    c: Coincident(g8,g-8)
    c: Equal(g6,g7)
    c: Equal(g7,g8)
    c: Vertical(g6)
    c: Horizontal(g-4,g2)
    c: Horizontal(g0,g-7)
FEATURE [PartDesign::Pocket] Pocket057
  BaseFeature = -> Pad043
  Direction = (1,-5e-16,5e-16)
  Length = 0
  Length2 = 5
  Offset = -1.6
  Placement = pos=(0,0,0) rot=(0.57735,0.57735,0.57735;2.0944rad)
  Profile = -> Sketch117
  ReferenceAxis = -> Sketch117 [N_Axis]
  Type = 3
  UpToFace = -> Pad043 [Face13]
FEATURE [Sketcher::SketchObject] Sketch118
  ExternalGeometry = -> [Pocket057]
  FullyConstrained = true
  MapMode = 5
  Placement = pos=(-1e-16,0,0) rot=(0.57735,0.57735,0.57735;2.0944rad)
  Support = -> [Pocket057]
  sketch-geometry (5):
    g0: Circle CenterX=-15 CenterY=56.45 CenterZ=0 NormalX=0 NormalY=0 NormalZ=1 AngleXU=0 Radius=1.65
    g1: Circle CenterX=15 CenterY=56.45 CenterZ=0 NormalX=0 NormalY=0 NormalZ=1 AngleXU=0 Radius=1.65
    g2: Circle CenterX=22.4 CenterY=7.2 CenterZ=0 NormalX=0 NormalY=0 NormalZ=1 AngleXU=0 Radius=1.7
    g3: Circle CenterX=-20.9 CenterY=46.1 CenterZ=0 NormalX=0 NormalY=0 NormalZ=1 AngleXU=0 Radius=1.7
    g4: Circle CenterX=2 CenterY=25.1 CenterZ=0 NormalX=0 NormalY=0 NormalZ=1 AngleXU=0 Radius=20
  constraints (13):
    c: Coincident(g0,g-4)
    c: Coincident(g1,g-3)
    c: Equal(g1,g0)
    c: Diameter(g1) = 3.3
    c: Diameter(g2) = 3.4
    c: DistanceX(g2,g-5) = 5.1
    c: DistanceY(g-5,g2) = 7.2
    c: DistanceY(g3,g-6) = 7.5
    c: Equal(g3,g2)
    c: DistanceX(g-7,g3) = 6.6
    c: DistanceX(g4,g-5) = 25.5
    c: DistanceY(g4,g-6) = 28.5
    c: Diameter(g4) = 40
FEATURE [PartDesign::Pocket] Pocket058
  BaseFeature = -> Pocket057
  Direction = (-1,9e-16,-6e-16)
  Length = 0
  Length2 = 5
  Placement = pos=(0,0,0) rot=(0.57735,0.57735,0.57735;2.0944rad)
  Profile = -> Sketch118
  ReferenceAxis = -> Sketch118 [N_Axis]
  Type = 3
  UpToFace = -> Pocket057 [Face5]
FEATURE [Sketcher::SketchObject] Sketch119
  AttachmentOffset = pos=(0,0,0) rot=(0,0,1;3.14159rad)
  ExternalGeometry = -> [Pocket058]
  FullyConstrained = true
  MapMode = 5
  Placement = pos=(-1.21e-14,-27.5,6.1e-15) rot=(-0.57735,0.57735,-0.57735;4.18879rad)
  Support = -> [Pocket058]
  sketch-geometry (4):
    g0: LineSegment StartX=-2.2e-15 StartY=15 StartZ=0 EndX=22.434 EndY=15 EndZ=0
    g1: LineSegment StartX=22.434 StartY=15 StartZ=0 EndX=12.9 EndY=7 EndZ=0
    g2: LineSegment StartX=12.9 StartY=7 StartZ=0 EndX=-1.8e-15 EndY=7 EndZ=0
    g3: LineSegment StartX=-2.2e-15 StartY=7 StartZ=0 EndX=-2.2e-15 EndY=15 EndZ=0
  constraints (11):
    c: Horizontal(g0)
    c: Coincident(g0,g1)
    c: Coincident(g1,g2)
    c: Horizontal(g2)
    c: Coincident(g2,g3)
    c: Coincident(g3,g0)
    c: Vertical(g3)
    c: Angle(g1,g2) = 2.44346
    c: Distance(g3) = 8
    c: Distance(g2) = 12.9
    c: Coincident(g0,g-3)
FEATURE [PartDesign::Pocket] Pocket059  label="风扇安装座002"
  BaseFeature = -> Pocket058
  Direction = (4e-16,1,-8e-16)
  Length = 5
  Length2 = 5
  Placement = pos=(0,0,0) rot=(0.57735,0.57735,0.57735;2.0944rad)
  Profile = -> Sketch119
  ReferenceAxis = -> Sketch119 [N_Axis]
  Type = 0
FEATURE [Sketcher::SketchObject] Sketch128
  FullyConstrained = true
  MapMode = 5
  Placement = pos=(0,0,0) rot=(1,0,0;1.5708rad)
  Support = -> [XZ_Plane023]
  sketch-geometry (8):
    g0: LineSegment StartX=-25 StartY=-15.95 StartZ=0 EndX=-45 EndY=-15.95 EndZ=0
    g1: LineSegment StartX=-45 StartY=-15.95 StartZ=0 EndX=-17.2 EndY=0 EndZ=0
    g2: LineSegment StartX=3.25476 StartY=0 StartZ=0 EndX=-17.2 EndY=0 EndZ=0
    g3: GeomPoint X=-15.6 Y=0 Z=0
    g4: LineSegment StartX=-25 StartY=-15.95 StartZ=0 EndX=-25 EndY=-17.25 EndZ=0
    g5: GeomPoint X=-1.6 Y=0 Z=0
    g6: LineSegment StartX=0 StartY=0 StartZ=0 EndX=0.786541 EndY=-1.39332 EndZ=0
    g7: LineSegment StartX=3.25476 StartY=0 StartZ=0 EndX=-25 EndY=-15.95 EndZ=0
  constraints (22):
    c: PointOnObject(g2,g-1)
    c: Horizontal(g0)
    c: Coincident(g0,g1)
    c: Coincident(g2,g1)
    c: Horizontal(g2)
    c: DistanceX(g0,g0) = 20
    c: PointOnObject(g3,g2)
    c: DistanceX(g1,g3) = 1.6
    c: Vertical(g4)
    c: Distance(g4) = 1.3
    c: PointOnObject(g5,g2)
    c: DistanceX(g5,g-1) = 1.6
    c: DistanceX(g3,g5) = 14
    c: DistanceX(g0,g-1) = 25
    c: Coincident(g6,g-1)
    c: Coincident(g7,g2)
    c: Coincident(g7,g0)
    c: PointOnObject(g6,g7)
    c: Distance(g6) = 1.6
    c: DistanceY(g4,g6) = 17.25
    c: Coincident(g0,g4)
    c: Perpendicular(g6,g7)
FEATURE [PartDesign::Pad] Pad047
  Direction = (0,-1,-2e-16)
  Length = 27.5
  Length2 = 10
  Placement = pos=(0,0,0) rot=(1,0,0;1.5708rad)
  Profile = -> Sketch128
  ReferenceAxis = -> Sketch128 [N_Axis]
  Type = 0
FEATURE [Sketcher::SketchObject] Sketch129
  ExternalGeometry = -> [Pad047]
  FullyConstrained = true
  MapMode = 5
  Placement = pos=(0,0,0) rot=(0.57735,0.57735,0.57735;2.0944rad)
  Support = -> [YZ_Plane023]
  sketch-geometry (11):
    g0: LineSegment StartX=-27.5 StartY=-9.42169 StartZ=0 EndX=-13.5 EndY=-15.95 EndZ=0
    g1: LineSegment StartX=-13.5 StartY=-15.95 StartZ=0 EndX=-13.5 EndY=0 EndZ=0
    g2: LineSegment StartX=-13.5 StartY=0 StartZ=0 EndX=0 EndY=0 EndZ=0
    g3: LineSegment StartX=0 StartY=0 StartZ=0 EndX=-4.9e-15 EndY=-15.95 EndZ=0
    g4: LineSegment StartX=-4.9e-15 StartY=-15.95 StartZ=0 EndX=0 EndY=-16.6571 EndZ=0
    g5: LineSegment StartX=0 StartY=-16.6571 StartZ=0 EndX=-28.2071 EndY=-16.6571 EndZ=0
    g6: LineSegment StartX=-28.2071 StartY=-16.6571 StartZ=0 EndX=-28.2071 EndY=0 EndZ=0
    g7: LineSegment StartX=-28.2071 StartY=0 StartZ=0 EndX=-27.5 EndY=-1.46e-14 EndZ=0
    g8: LineSegment StartX=-27.5 StartY=-1.46e-14 StartZ=0 EndX=-27.5 EndY=-9.42169 EndZ=0
    g9: LineSegment StartX=-27.5 StartY=-15.95 StartZ=0 EndX=-27.5 EndY=-16.6571 EndZ=0
    g10: LineSegment StartX=-27.5 StartY=-15.95 StartZ=0 EndX=-28.2071 EndY=-15.95 EndZ=0
  constraints (31):
    c: PointOnObject(g0,g-3)
    c: PointOnObject(g0,g-4)
    c: Coincident(g0,g1)
    c: PointOnObject(g1,g-1)
    c: Vertical(g1)
    c: Coincident(g1,g2)
    c: Coincident(g2,g-1)
    c: Coincident(g2,g3)
    c: Coincident(g3,g-4)
    c: Coincident(g3,g4)
    c: PointOnObject(g4,g-2)
    c: Coincident(g4,g5)
    c: Horizontal(g5)
    c: Coincident(g5,g6)
    c: PointOnObject(g6,g-1)
    c: Vertical(g6)
    c: Coincident(g6,g7)
    c: Coincident(g7,g-3)
    c: Coincident(g7,g8)
    c: Coincident(g8,g0)
    c: Angle(g0,g8) = 2.00713
    c: Angle(g0,g-4) = 0.436332
    c: DistanceX(g7,g1) = 14
    c: Coincident(g9,g-4)
    c: PointOnObject(g9,g5)
    c: Vertical(g9)
    c: Coincident(g10,g9)
    c: PointOnObject(g10,g6)
    c: Horizontal(g10)
    c: Equal(g10,g9)
    c: Distance(g9,g5) = 1
FEATURE [PartDesign::Pocket] Pocket065
  BaseFeature = -> Pad047
  Direction = (-1,2e-16,-3e-16)
  Length = 50
  Length2 = 20
  Placement = pos=(0,0,0) rot=(1,0,0;1.5708rad)
  Profile = -> Sketch129
  ReferenceAxis = -> Sketch129 [N_Axis]
  Type = 4
FEATURE [PartDesign::Thickness] Thickness
  Base = -> Pocket065 [Face3,Face6]
  BaseFeature = -> Pocket065
  Intersection = false
  Join = 1
  Mode = 2
  Reversed = true
  SupportTransform = false
  Value = 1.6
FEATURE [Sketcher::SketchObject] Sketch130
  ExternalGeometry = -> [Thickness]
  FullyConstrained = true
  MapMode = 5
  Placement = pos=(-3e-15,-13.5,5.9e-15) rot=(0,0.707107,0.707107;3.14159rad)
  Support = -> [Thickness]
  sketch-geometry (4):
    g0: LineSegment StartX=13.9849 StartY=-0.58241 StartZ=0 EndX=15 EndY=-0.58241 EndZ=0
    g1: LineSegment StartX=15 StartY=-0.58241 StartZ=0 EndX=15 EndY=-1.24e-14 EndZ=0
    g2: LineSegment StartX=15 StartY=-1.24e-14 StartZ=0 EndX=13.9849 EndY=-1.24e-14 EndZ=0
    g3: LineSegment StartX=13.9849 StartY=-1.24e-14 StartZ=0 EndX=13.9849 EndY=-0.58241 EndZ=0
  constraints (11):
    c: Coincident(g0,g1)
    c: Coincident(g1,g2)
    c: Coincident(g2,g3)
    c: Coincident(g3,g0)
    c: Horizontal(g0)
    c: Horizontal(g2)
    c: Vertical(g1)
    c: Vertical(g3)
    c: DistanceX(g-4,g1) = 15
    c: PointOnObject(g0,g-3)
    c: Coincident(g-3,g2)
FEATURE [PartDesign::Pocket] Pocket066
  BaseFeature = -> Thickness
  Direction = (-2e-16,-1,2e-16)
  Length = 0
  Length2 = 5
  Profile = -> Sketch130
  ReferenceAxis = -> Sketch130 [N_Axis]
  Type = 3
  UpToFace = -> Thickness [Face10]
FEATURE [Sketcher::SketchObject] Sketch131
  ExternalGeometry = -> [Pocket066]
  FullyConstrained = true
  MapMode = 5
  Placement = pos=(-3e-15,-13.5,5.9e-15) rot=(0,0.707107,0.707107;3.14159rad)
  Support = -> [Pocket066]
  sketch-geometry (4):
    g0: LineSegment StartX=-3.25476 StartY=0 StartZ=0 EndX=-1.6 EndY=0 EndZ=0
    g1: LineSegment StartX=-1.6 StartY=0 StartZ=0 EndX=-1.6 EndY=-0.934121 EndZ=0
    g2: LineSegment StartX=-1.6 StartY=-0.934121 StartZ=0 EndX=-3.25476 EndY=-0.934121 EndZ=0
    g3: LineSegment StartX=-3.25476 StartY=-0.934121 StartZ=0 EndX=-3.25476 EndY=0 EndZ=0
  constraints (11):
    c: Coincident(g0,g1)
    c: Coincident(g1,g2)
    c: Coincident(g2,g3)
    c: Coincident(g3,g0)
    c: Horizontal(g0)
    c: Horizontal(g2)
    c: Vertical(g1)
    c: Vertical(g3)
    c: Coincident(g0,g-3)
    c: PointOnObject(g1,g-3)
    c: DistanceX(g0,g-1) = 1.6
FEATURE [PartDesign::Pocket] Pocket067
  BaseFeature = -> Pocket066
  Direction = (-2e-16,-1,2e-16)
  Length = 5
  Length2 = 5
  Profile = -> Sketch131
  ReferenceAxis = -> Sketch131 [N_Axis]
  Type = 1
FEATURE [Sketcher::SketchObject] Sketch132
  ExternalGeometry = -> [Pocket067]
  FullyConstrained = true
  MapMode = 5
  Placement = pos=(-3e-15,-13.5,5.9e-15) rot=(0,0.707107,0.707107;3.14159rad)
  Support = -> [Pocket067]
  sketch-geometry (5):
    g0: LineSegment StartX=-1.28e-14 StartY=-1.7e-15 StartZ=0 EndX=21.5845 EndY=-12.1846 EndZ=0
    g1: LineSegment StartX=21.5845 StartY=-12.1846 StartZ=0 EndX=35.222 EndY=-12.1846 EndZ=0
    g2: LineSegment StartX=35.222 StartY=-12.1846 StartZ=0 EndX=15 EndY=-0.58241 EndZ=0
    g3: LineSegment StartX=15 StartY=-0.58241 StartZ=0 EndX=15 EndY=-1.24e-14 EndZ=0
    g4: LineSegment StartX=15 StartY=-1.24e-14 StartZ=0 EndX=-1.24e-14 EndY=-1.7e-15 EndZ=0
  constraints (12):
    c: Coincident(g-5,g0)
    c: PointOnObject(g0,g-5)
    c: Coincident(g0,g1)
    c: PointOnObject(g1,g-3)
    c: Horizontal(g1)
    c: Coincident(g1,g2)
    c: Coincident(g2,g-4)
    c: Coincident(g2,g3)
    c: Coincident(g3,g-4)
    c: Coincident(g3,g4)
    c: Coincident(g4,g0)
    c: DistanceY(g-5,g0) = 2
FEATURE [PartDesign::Pad] Pad048
  BaseFeature = -> Pocket067
  Direction = (2e-16,1,-2e-16)
  Length = 1.6
  Length2 = 10
  Profile = -> Sketch132
  ReferenceAxis = -> Sketch132 [N_Axis]
  Reversed = true
  Type = 0
FEATURE [PartDesign::Fillet] Fillet
  Base = -> Pad048 [Edge35]
  BaseFeature = -> Pad048
  Radius = 4
  SupportTransform = false
  UseAllEdges = false
FEATURE [PartDesign::Chamfer] Chamfer
  Angle = 67.3
  Base = -> Fillet [Edge43]
  BaseFeature = -> Fillet
  ChamferType = 2
  FlipDirection = false
  Size = 2.8
  Size2 = 1
  SupportTransform = false
  UseAllEdges = false
FEATURE [PartDesign::Chamfer] Chamfer001
  Angle = 90
  Base = -> Chamfer [Edge2]
  BaseFeature = -> Chamfer
  ChamferType = 2
  FlipDirection = false
  Size = 1.5
  Size2 = 1
  SupportTransform = false
  UseAllEdges = false
FEATURE [PartDesign::Fillet] Fillet001
  Base = -> Chamfer001 [Edge56]
  BaseFeature = -> Chamfer001
  Radius = 1.5
  SupportTransform = false
  UseAllEdges = false
FEATURE [Sketcher::SketchObject] Sketch133
  ExternalGeometry = -> [Fillet001]
  FullyConstrained = true
  MapMode = 5
  Placement = pos=(-3.8e-15,-15.1,4.4e-15) rot=(1,0,0;1.5708rad)
  Support = -> [Fillet001]
  sketch-geometry (3):
    g0: LineSegment StartX=-15 StartY=-1.28e-14 StartZ=0 EndX=-15 EndY=-8.4676 EndZ=0
    g1: LineSegment StartX=-15 StartY=-8.4676 StartZ=0 EndX=1.24e-14 EndY=-3.6e-15 EndZ=0
    g2: LineSegment StartX=1.24e-14 StartY=-3.6e-15 StartZ=0 EndX=-15 EndY=-1.28e-14 EndZ=0
  constraints (7):
    c: Coincident(g-3,g0)
    c: PointOnObject(g0,g-4)
    c: Vertical(g0)
    c: Coincident(g0,g1)
    c: Coincident(g1,g-4)
    c: Coincident(g1,g2)
    c: Coincident(g2,g0)
FEATURE [PartDesign::Pocket] Pocket068
  BaseFeature = -> Fillet001
  Direction = (3e-16,1,-2e-16)
  Length = 5
  Length2 = 5
  Profile = -> Sketch133
  ReferenceAxis = -> Sketch133 [N_Axis]
  Type = 1
FEATURE [Sketcher::SketchObject] Sketch134
  ExternalGeometry = -> [Pocket068]
  FullyConstrained = true
  MapMode = 5
  Placement = pos=(-3.4e-15,-13.5,3.9e-15) rot=(0,0.707107,0.707107;3.14159rad)
  Support = -> [Pocket068]
  sketch-geometry (7):
    g0: LineSegment StartX=-1.24e-14 StartY=-1.8e-15 StartZ=0 EndX=-1.6 EndY=1e-16 EndZ=0
    g1: LineSegment StartX=-1.6 StartY=1e-16 StartZ=0 EndX=-1.6 EndY=-0.934121 EndZ=0
    g2: LineSegment StartX=-1.6 StartY=-0.934121 StartZ=0 EndX=16.6 EndY=-11.2081 EndZ=0
    g3: LineSegment StartX=16.6 StartY=-11.2081 StartZ=0 EndX=16.6 EndY=-5.3e-15 EndZ=0
    g4: LineSegment StartX=16.6 StartY=-5.3e-15 StartZ=0 EndX=15 EndY=-4.5e-15 EndZ=0
    g5: LineSegment StartX=15 StartY=-4.5e-15 StartZ=0 EndX=15 EndY=-8.4676 EndZ=0
    g6: LineSegment StartX=15 StartY=-8.4676 StartZ=0 EndX=-1.24e-14 EndY=-1.8e-15 EndZ=0
  constraints (16):
    c: Coincident(g-4,g0)
    c: Coincident(g0,g-3)
    c: Coincident(g0,g1)
    c: Coincident(g1,g-8)
    c: Coincident(g1,g2)
    c: PointOnObject(g2,g-8)
    c: Coincident(g2,g3)
    c: PointOnObject(g3,g-6)
    c: Vertical(g3)
    c: Coincident(g3,g4)
    c: Coincident(g4,g-6)
    c: Coincident(g4,g5)
    c: Coincident(g5,g-4)
    c: Coincident(g5,g6)
    c: Coincident(g6,g0)
    c: DistanceX(g4,g3) = 1.6
FEATURE [Sketcher::SketchObject] Sketch135
  FullyConstrained = true
  MapMode = 5
  Placement = pos=(0,0,0) rot=(1,0,0;1.5708rad)
  Support = -> [XZ_Plane024]
  sketch-geometry (8):
    g0: LineSegment StartX=-25 StartY=-15.95 StartZ=0 EndX=-45 EndY=-15.95 EndZ=0
    g1: LineSegment StartX=-45 StartY=-15.95 StartZ=0 EndX=-17.2 EndY=0 EndZ=0
    g2: LineSegment StartX=3.25476 StartY=0 StartZ=0 EndX=-17.2 EndY=0 EndZ=0
    g3: GeomPoint X=-15.6 Y=0 Z=0
    g4: LineSegment StartX=-25 StartY=-15.95 StartZ=0 EndX=-25 EndY=-17.25 EndZ=0
    g5: GeomPoint X=-1.6 Y=0 Z=0
    g6: LineSegment StartX=0 StartY=0 StartZ=0 EndX=0.786541 EndY=-1.39332 EndZ=0
    g7: LineSegment StartX=3.25476 StartY=0 StartZ=0 EndX=-25 EndY=-15.95 EndZ=0
  constraints (22):
    c: PointOnObject(g2,g-1)
    c: Horizontal(g0)
    c: Coincident(g0,g1)
    c: Coincident(g2,g1)
    c: Horizontal(g2)
    c: DistanceX(g0,g0) = 20
    c: PointOnObject(g3,g2)
    c: DistanceX(g1,g3) = 1.6
    c: Vertical(g4)
    c: Distance(g4) = 1.3
    c: PointOnObject(g5,g2)
    c: DistanceX(g5,g-1) = 1.6
    c: DistanceX(g3,g5) = 14
    c: DistanceX(g0,g-1) = 25
    c: Coincident(g6,g-1)
    c: Coincident(g7,g2)
    c: Coincident(g7,g0)
    c: PointOnObject(g6,g7)
    c: Perpendicular(g7,g6)
    c: Distance(g6) = 1.6
    c: DistanceY(g4,g6) = 17.25
    c: Coincident(g0,g4)
FEATURE [PartDesign::Pad] Pad050
  Direction = (0,-1,-2e-16)
  Length = 27.5
  Length2 = 10
  Placement = pos=(0,0,0) rot=(1,0,0;1.5708rad)
  Profile = -> Sketch135
  ReferenceAxis = -> Sketch135 [N_Axis]
  Type = 0
FEATURE [Sketcher::SketchObject] Sketch136
  ExternalGeometry = -> [Pad050]
  FullyConstrained = true
  MapMode = 5
  Placement = pos=(0,0,0) rot=(0.57735,0.57735,0.57735;2.0944rad)
  Support = -> [YZ_Plane024]
  sketch-geometry (11):
    g0: LineSegment StartX=-27.5 StartY=-9.42169 StartZ=0 EndX=-13.5 EndY=-15.95 EndZ=0
    g1: LineSegment StartX=-13.5 StartY=-15.95 StartZ=0 EndX=-13.5 EndY=0 EndZ=0
    g2: LineSegment StartX=-13.5 StartY=0 StartZ=0 EndX=0 EndY=0 EndZ=0
    g3: LineSegment StartX=0 StartY=0 StartZ=0 EndX=-4.9e-15 EndY=-15.95 EndZ=0
    g4: LineSegment StartX=-4.9e-15 StartY=-15.95 StartZ=0 EndX=0 EndY=-16.6571 EndZ=0
    g5: LineSegment StartX=0 StartY=-16.6571 StartZ=0 EndX=-28.2071 EndY=-16.6571 EndZ=0
    g6: LineSegment StartX=-28.2071 StartY=-16.6571 StartZ=0 EndX=-28.2071 EndY=0 EndZ=0
    g7: LineSegment StartX=-28.2071 StartY=0 StartZ=0 EndX=-27.5 EndY=-1.46e-14 EndZ=0
    g8: LineSegment StartX=-27.5 StartY=-1.46e-14 StartZ=0 EndX=-27.5 EndY=-9.42169 EndZ=0
    g9: LineSegment StartX=-27.5 StartY=-15.95 StartZ=0 EndX=-27.5 EndY=-16.6571 EndZ=0
    g10: LineSegment StartX=-27.5 StartY=-15.95 StartZ=0 EndX=-28.2071 EndY=-15.95 EndZ=0
  constraints (31):
    c: PointOnObject(g0,g-3)
    c: PointOnObject(g0,g-4)
    c: Coincident(g0,g1)
    c: PointOnObject(g1,g-1)
    c: Vertical(g1)
    c: Coincident(g1,g2)
    c: Coincident(g2,g-1)
    c: Coincident(g2,g3)
    c: Coincident(g3,g-4)
    c: Coincident(g3,g4)
    c: PointOnObject(g4,g-2)
    c: Coincident(g4,g5)
    c: Horizontal(g5)
    c: Coincident(g5,g6)
    c: PointOnObject(g6,g-1)
    c: Vertical(g6)
    c: Coincident(g6,g7)
    c: Coincident(g7,g-3)
    c: Coincident(g7,g8)
    c: Coincident(g8,g0)
    c: Angle(g0,g8) = 2.00713
    c: Angle(g0,g-4) = 0.436332
    c: DistanceX(g7,g1) = 14
    c: Coincident(g9,g-4)
    c: PointOnObject(g9,g5)
    c: Vertical(g9)
    c: Coincident(g10,g9)
    c: PointOnObject(g10,g6)
    c: Horizontal(g10)
    c: Equal(g9,g10)
    c: Distance(g9,g5) = 1
FEATURE [PartDesign::Pocket] Pocket069
  BaseFeature = -> Pad050
  Direction = (-1,2e-16,-3e-16)
  Length = 50
  Length2 = 20
  Placement = pos=(0,0,0) rot=(1,0,0;1.5708rad)
  Profile = -> Sketch136
  ReferenceAxis = -> Sketch136 [N_Axis]
  Type = 4
FEATURE [PartDesign::Thickness] Thickness001
  Base = -> Pocket069 [Face3,Face6]
  BaseFeature = -> Pocket069
  Intersection = false
  Join = 1
  Mode = 2
  Reversed = true
  SupportTransform = false
  Value = 1.6
FEATURE [Sketcher::SketchObject] Sketch137
  ExternalGeometry = -> [Thickness001]
  FullyConstrained = true
  MapMode = 5
  Placement = pos=(-3e-15,-13.5,5.9e-15) rot=(0,0.707107,0.707107;3.14159rad)
  Support = -> [Thickness001]
  sketch-geometry (4):
    g0: LineSegment StartX=13.9849 StartY=-0.58241 StartZ=0 EndX=15 EndY=-0.58241 EndZ=0
    g1: LineSegment StartX=15 StartY=-0.58241 StartZ=0 EndX=15 EndY=-1.24e-14 EndZ=0
    g2: LineSegment StartX=15 StartY=-1.24e-14 StartZ=0 EndX=13.9849 EndY=-1.24e-14 EndZ=0
    g3: LineSegment StartX=13.9849 StartY=-1.24e-14 StartZ=0 EndX=13.9849 EndY=-0.58241 EndZ=0
  constraints (11):
    c: Coincident(g0,g1)
    c: Coincident(g1,g2)
    c: Coincident(g2,g3)
    c: Coincident(g3,g0)
    c: Horizontal(g0)
    c: Horizontal(g2)
    c: Vertical(g1)
    c: Vertical(g3)
    c: DistanceX(g-4,g1) = 15
    c: PointOnObject(g0,g-3)
    c: Coincident(g-3,g2)
FEATURE [PartDesign::Pocket] Pocket070
  BaseFeature = -> Thickness001
  Direction = (-2e-16,-1,2e-16)
  Length = 0
  Length2 = 5
  Profile = -> Sketch137
  ReferenceAxis = -> Sketch137 [N_Axis]
  Type = 3
  UpToFace = -> Thickness001 [Face10]
FEATURE [Sketcher::SketchObject] Sketch138
  ExternalGeometry = -> [Pocket070]
  FullyConstrained = true
  MapMode = 5
  Placement = pos=(-3e-15,-13.5,5.9e-15) rot=(0,0.707107,0.707107;3.14159rad)
  Support = -> [Pocket070]
  sketch-geometry (4):
    g0: LineSegment StartX=-3.25476 StartY=0 StartZ=0 EndX=-1.6 EndY=0 EndZ=0
    g1: LineSegment StartX=-1.6 StartY=0 StartZ=0 EndX=-1.6 EndY=-0.934121 EndZ=0
    g2: LineSegment StartX=-1.6 StartY=-0.934121 StartZ=0 EndX=-3.25476 EndY=-0.934121 EndZ=0
    g3: LineSegment StartX=-3.25476 StartY=-0.934121 StartZ=0 EndX=-3.25476 EndY=0 EndZ=0
  constraints (11):
    c: Coincident(g0,g1)
    c: Coincident(g1,g2)
    c: Coincident(g2,g3)
    c: Coincident(g3,g0)
    c: Horizontal(g0)
    c: Horizontal(g2)
    c: Vertical(g1)
    c: Vertical(g3)
    c: Coincident(g0,g-3)
    c: PointOnObject(g1,g-3)
    c: DistanceX(g0,g-1) = 1.6
FEATURE [PartDesign::Pocket] Pocket071
  BaseFeature = -> Pocket070
  Direction = (-2e-16,-1,2e-16)
  Length = 5
  Length2 = 5
  Profile = -> Sketch138
  ReferenceAxis = -> Sketch138 [N_Axis]
  Type = 1
FEATURE [Sketcher::SketchObject] Sketch139
  ExternalGeometry = -> [Pocket071]
  FullyConstrained = true
  MapMode = 5
  Placement = pos=(-3e-15,-13.5,5.9e-15) rot=(0,0.707107,0.707107;3.14159rad)
  Support = -> [Pocket071]
  sketch-geometry (5):
    g0: LineSegment StartX=1.71341e-07 StartY=-9.67168e-08 StartZ=0 EndX=21.5845 EndY=-12.1846 EndZ=0
    g1: LineSegment StartX=21.5845 StartY=-12.1846 StartZ=0 EndX=35.222 EndY=-12.1846 EndZ=0
    g2: LineSegment StartX=35.222 StartY=-12.1846 StartZ=0 EndX=15 EndY=-0.58241 EndZ=0
    g3: LineSegment StartX=15 StartY=-0.58241 StartZ=0 EndX=15 EndY=-1.24e-14 EndZ=0
    g4: LineSegment StartX=15 StartY=-1.24e-14 StartZ=0 EndX=1.71341e-07 EndY=-9.67168e-08 EndZ=0
  constraints (12):
    c: Coincident(g-5,g0)
    c: PointOnObject(g0,g-5)
    c: Coincident(g0,g1)
    c: PointOnObject(g1,g-3)
    c: Horizontal(g1)
    c: Coincident(g1,g2)
    c: Coincident(g2,g-4)
    c: Coincident(g2,g3)
    c: Coincident(g3,g-4)
    c: Coincident(g3,g4)
    c: Coincident(g4,g0)
    c: DistanceY(g-5,g0) = 2
FEATURE [PartDesign::Pad] Pad051
  BaseFeature = -> Pocket071
  Direction = (2e-16,1,-2e-16)
  Length = 1.6
  Length2 = 10
  Profile = -> Sketch139
  ReferenceAxis = -> Sketch139 [N_Axis]
  Reversed = true
  Type = 0
FEATURE [PartDesign::Fillet] Fillet002
  Base = -> Pad051 [Edge35]
  BaseFeature = -> Pad051
  Radius = 4
  SupportTransform = false
  UseAllEdges = false
FEATURE [PartDesign::Chamfer] Chamfer002
  Angle = 67.3
  Base = -> Fillet002 [Edge43]
  BaseFeature = -> Fillet002
  ChamferType = 2
  FlipDirection = false
  Size = 2.8
  Size2 = 1
  SupportTransform = false
  UseAllEdges = false
FEATURE [PartDesign::Chamfer] Chamfer003
  Angle = 90
  Base = -> Chamfer002 [Edge2]
  BaseFeature = -> Chamfer002
  ChamferType = 2
  FlipDirection = false
  Size = 1.5
  Size2 = 1
  SupportTransform = false
  UseAllEdges = false
FEATURE [PartDesign::Fillet] Fillet003
  Base = -> Chamfer003 [Edge56]
  BaseFeature = -> Chamfer003
  Radius = 1.5
  SupportTransform = false
  UseAllEdges = false
FEATURE [Sketcher::SketchObject] Sketch140
  ExternalGeometry = -> [Fillet003]
  FullyConstrained = true
  MapMode = 5
  Placement = pos=(-3.8e-15,-15.1,4.4e-15) rot=(1,0,0;1.5708rad)
  Support = -> [Fillet003]
  sketch-geometry (3):
    g0: LineSegment StartX=-15 StartY=-1.28e-14 StartZ=0 EndX=-15 EndY=-8.4676 EndZ=0
    g1: LineSegment StartX=-15 StartY=-8.4676 StartZ=0 EndX=-1.71341e-07 EndY=-9.67168e-08 EndZ=0
    g2: LineSegment StartX=-1.71341e-07 StartY=-9.67168e-08 StartZ=0 EndX=-15 EndY=-1.28e-14 EndZ=0
  constraints (7):
    c: Coincident(g-3,g0)
    c: PointOnObject(g0,g-4)
    c: Vertical(g0)
    c: Coincident(g0,g1)
    c: Coincident(g1,g-4)
    c: Coincident(g1,g2)
    c: Coincident(g2,g0)
FEATURE [PartDesign::Pocket] Pocket072
  BaseFeature = -> Fillet003
  Direction = (3e-16,1,-2e-16)
  Length = 5
  Length2 = 5
  Profile = -> Sketch140
  ReferenceAxis = -> Sketch140 [N_Axis]
  Type = 1
FEATURE [Sketcher::SketchObject] Sketch146
  ExternalGeometry = -> [Pocket059]
  FullyConstrained = true
  MapMode = 5
  Placement = pos=(-1e-16,0,0) rot=(0.57735,0.57735,0.57735;2.0944rad)
  Support = -> [Pocket059]
  sketch-geometry (11):
    g0: ArcOfCircle CenterX=8 CenterY=25.1 CenterZ=0 NormalX=0 NormalY=0 NormalZ=1 AngleXU=0 Radius=6 StartAngle=2.00713 EndAngle=3.14159
    g1: ArcOfCircle CenterX=11.0114 CenterY=39.7448 CenterZ=0 NormalX=0 NormalY=0 NormalZ=1 AngleXU=0 Radius=6 StartAngle=5.14872 EndAngle=6.06906
    g2: LineSegment StartX=5.46429 StartY=30.5378 StartZ=0 EndX=13.5471 EndY=34.3069 EndZ=0
    g3: ArcOfCircle CenterX=2 CenterY=25.1 CenterZ=0 NormalX=0 NormalY=0 NormalZ=1 AngleXU=0 Radius=20 StartAngle=4.71239 EndAngle=4.93933
    g4: ArcOfCircle CenterX=-20.9209 CenterY=3.52811 CenterZ=0 NormalX=0 NormalY=0 NormalZ=1 AngleXU=0 Radius=27.5 StartAngle=0.0758806 EndAngle=0.420763
    g5: LineSegment StartX=2 StartY=25.1 StartZ=0 EndX=2 EndY=5.1 EndZ=0
    g6: ArcOfCircle CenterX=9.65718 CenterY=17.2114 CenterZ=0 NormalX=0 NormalY=0 NormalZ=1 AngleXU=0 Radius=6 StartAngle=2.33625 EndAngle=3.56236
    g7: ArcOfCircle CenterX=24.5537 CenterY=1.70843 CenterZ=0 NormalX=0 NormalY=0 NormalZ=1 AngleXU=0 Radius=27.5 StartAngle=2.02708 EndAngle=2.33625
    g8: ArcOfCircle CenterX=7.59021 CenterY=36.2698 CenterZ=0 NormalX=0 NormalY=0 NormalZ=1 AngleXU=0 Radius=11 StartAngle=5.16867 EndAngle=6.28319
    g9: ArcOfCircle CenterX=2 CenterY=25.1 CenterZ=0 NormalX=0 NormalY=0 NormalZ=1 AngleXU=0 Radius=20 StartAngle=0.592565 EndAngle=0.732178
    g10: LineSegment StartX=5.5 StartY=21.5378 StartZ=0 EndX=12.4369 EndY=26.3951 EndZ=0
  constraints (31):
    c: Coincident(g0,g-3)
    c: PointOnObject(g1,g-3)
    c: Coincident(g3,g0)
    c: PointOnObject(g3,g-3)
    c: Coincident(g3,g4)
    c: Coincident(g5,g3)
    c: Vertical(g5)
    c: Coincident(g9,g0)
    c: Coincident(g9,g1)
    c: Coincident(g9,g8)
    c: Tangent(g8,g7) = 1.5708
    c: Tangent(g7,g6) = -1.5708
    c: Tangent(g6,g4) = 1.5708
    c: Equal(g4,g7)
    c: Tangent(g2,g1) = -1.5708
    c: Tangent(g2,g0) = 1.5708
    c: Coincident(g10,g6)
    c: Coincident(g10,g7)
    c: Angle(g-4,g10) = 0.610865
    c: Equal(g1,g0)
    c: Equal(g0,g6)
    c: DistanceX(g3,g3) = 4.5
    c: Tangent(g5,g0) = -1.5708
    c: DistanceY(g6,g0) = 9
    c: Diameter(g4) = 55
    c: Radius(g0) = 6
    c: Radius(g8) = 11
    c: Horizontal(g8,g8)
    c: Angle(g-1,g2) = 0.436332
    c: DistanceY(g8,g1) = 2.2
    c: DistanceX(g6,g3) = 1
FEATURE [PartDesign::Pad] Pad057  label="鱼尾纹"
  BaseFeature = -> Pocket059
  Direction = (1,-2e-16,2e-16)
  Length = 1.6
  Length2 = 10
  Placement = pos=(0,0,0) rot=(0.57735,0.57735,0.57735;2.0944rad)
  Profile = -> Sketch146
  ReferenceAxis = -> Sketch146 [N_Axis]
  Reversed = true
  Type = 3
  UpToFace = -> Pocket059 [Face27]
FEATURE [PartDesign::Mirrored] Mirrored
  BaseFeature = -> Pad057
  MirrorPlane = -> Pad057 [Face34]
  Originals = -> [Pad057]
  Placement = pos=(0,0,0) rot=(0.57735,0.57735,0.57735;2.0944rad)
FEATURE [PartDesign::Body] Body016  label="风扇安装座"
  Group = -> [Sketch116,Pad043,Sketch117,Pocket057,Sketch118,Pocket058,Sketch119,Pocket059,Sketch146,Pad057,Mirrored]
  Origin = -> Origin020
  Tip = -> Mirrored
FEATURE [Sketcher::SketchObject] Sketch143
  ExternalGeometry = -> [Pocket072]
  FullyConstrained = true
  MapMode = 2
  Support = -> [Pocket072]
  sketch-geometry (3):
    g0: ArcOfCircle CenterX=-6 CenterY=-19.9 CenterZ=0 NormalX=0 NormalY=0 NormalZ=1 AngleXU=0 Radius=6 StartAngle=4.71239 EndAngle=6.28319
    g1: LineSegment StartX=-1.42e-14 StartY=-19.9 StartZ=0 EndX=-1.42e-14 EndY=-25.9 EndZ=0
    g2: LineSegment StartX=-1.42e-14 StartY=-25.9 StartZ=0 EndX=-6 EndY=-25.9 EndZ=0
  constraints (7):
    c: Coincident(g1,g2)
    c: Horizontal(g2)
    c: Vertical(g1)
    c: Diameter(g0) = 12
    c: Coincident(g1,g-4)
    c: Tangent(g0,g1) = 1.5708
    c: Tangent(g2,g0) = 1.5708
FEATURE [PartDesign::Pad] Pad054
  BaseFeature = -> Pocket072
  Direction = (0,0,1)
  Length = 10
  Length2 = 10
  Profile = -> Sketch143
  ReferenceAxis = -> Sketch143 [N_Axis]
  Reversed = true
  Type = 3
  UpToFace = -> Pocket072 [Face11]
FEATURE [Sketcher::SketchObject] Sketch144
  FullyConstrained = false
  MapMode = 5
  Placement = pos=(0,-25.9,-5.7e-15) rot=(0,0.707107,0.707107;3.14159rad)
  Support = -> [Pad054]
  sketch-geometry (4):
    g0: LineSegment StartX=15 StartY=-3.8e-15 StartZ=0 EndX=15 EndY=-1.2 EndZ=0
    g1: LineSegment StartX=15 StartY=-1.2 StartZ=0 EndX=2.3703 EndY=-1.2 EndZ=0
    g2: LineSegment StartX=2.3703 StartY=-1.2 StartZ=0 EndX=1.92127e-07 EndY=-9.72672e-08 EndZ=0
    g3: LineSegment StartX=1.92127e-07 StartY=-9.72672e-08 StartZ=0 EndX=15 EndY=-3.8e-15 EndZ=0
  constraints (6):
    c: Coincident(g0,g1)
    c: Horizontal(g1)
    c: Coincident(g1,g2)
    c: Coincident(g2,g3)
    c: Coincident(g3,g0)
    c: DistanceY(g0,g0) = 1.2
FEATURE [PartDesign::Pad] Pad055
  BaseFeature = -> Pad054
  Direction = (0,1,2e-16)
  Length = 31.9
  Length2 = 10
  Profile = -> Sketch144
  ReferenceAxis = -> Sketch144 [N_Axis]
  Type = 0
FEATURE [Sketcher::SketchObject] Sketch145
  ExternalGeometry = -> [Pad055]
  FullyConstrained = true
  MapMode = 5
  Placement = pos=(-15,3.8e-15,0) rot=(0.57735,0.57735,0.57735;2.0944rad)
  Support = -> [Pad055]
  sketch-geometry (4):
    g0: LineSegment StartX=-15.1 StartY=-1.2 StartZ=0 EndX=-13.9 EndY=-1.2 EndZ=0
    g1: LineSegment StartX=-13.9 StartY=-1.2 StartZ=0 EndX=-13.9 EndY=-8.4676 EndZ=0
    g2: LineSegment StartX=-13.9 StartY=-8.4676 StartZ=0 EndX=-15.1 EndY=-8.4676 EndZ=0
    g3: LineSegment StartX=-15.1 StartY=-8.4676 StartZ=0 EndX=-15.1 EndY=-1.2 EndZ=0
  constraints (10):
    c: Coincident(g0,g1)
    c: Coincident(g1,g2)
    c: Coincident(g2,g3)
    c: Coincident(g3,g0)
    c: Horizontal(g0)
    c: Horizontal(g2)
    c: Vertical(g1)
    c: Coincident(g0,g-3)
    c: Coincident(g2,g-3)
    c: DistanceX(g0,g0) = 1.2
FEATURE [PartDesign::Pad] Pad056  label="优化搭桥"
  BaseFeature = -> Pad055
  Direction = (1,-1e-16,-1e-16)
  Length = 0.4
  Length2 = 10
  Offset = -6
  Profile = -> Sketch145
  ReferenceAxis = -> Sketch145 [N_Axis]
  Type = 0
FEATURE [Sketcher::SketchObject] Sketch147
  ExternalGeometry = -> [Pad055]
  FullyConstrained = true
  MapMode = 5
  Placement = pos=(0,-25.9,-5.7e-15) rot=(0,0.707107,0.707107;3.14159rad)
  Support = -> [Pad055]
  sketch-geometry (3):
    g0: LineSegment StartX=15 StartY=-1.2 StartZ=0 EndX=16.0764 EndY=-1.2 EndZ=0
    g1: LineSegment StartX=16.0764 StartY=-1.2 StartZ=0 EndX=15 EndY=-0.58241 EndZ=0
    g2: LineSegment StartX=15 StartY=-0.58241 StartZ=0 EndX=15 EndY=-1.2 EndZ=0
  constraints (7):
    c: Coincident(g-4,g0)
    c: PointOnObject(g0,g-3)
    c: Horizontal(g0)
    c: Coincident(g0,g1)
    c: Coincident(g1,g-4)
    c: Coincident(g1,g2)
    c: Coincident(g2,g0)
FEATURE [PartDesign::Pad] Pad058
  BaseFeature = -> Pad056
  Direction = (0,1,2e-16)
  Length = 10
  Length2 = 10
  Profile = -> Sketch147
  ReferenceAxis = -> Sketch147 [N_Axis]
  Type = 3
  UpToFace = -> Pad056 [Face2]
FEATURE [PartDesign::Body] Body019  label="右"
  Group = -> [Sketch135,Pad050,Sketch136,Pocket069,Thickness001,Sketch137,Pocket070,Sketch138,Pocket071,Sketch139,Pad051,Fillet002,Chamfer002,Chamfer003,Fillet003,Sketch140,Pocket072,Sketch143,Pad054,Sketch144,Pad055,Sketch145,Pad056,Sketch147,Pad058]
  Origin = -> Origin024
  Placement = pos=(-1.6,0,0) rot=(0,0,1;0rad)
  Tip = -> Pad058
  expr: .Placement.Base.x = -1.6
FEATURE [Part::Mirroring] Part__Mirroring  label="右 (Mirror #1)"
  Base = (-19.3152,-4.76837e-07,-7.225)
  Normal = (0,1,-1.19209e-07)
  Source = -> Body019
FEATURE [PartDesign::Pad] Pad049
  BaseFeature = -> Pocket068
  Direction = (3e-16,1,-2e-16)
  Length = 27
  Length2 = 10
  Profile = -> Sketch134
  ReferenceAxis = -> Sketch134 [N_Axis]
  Type = 3
  UpToFace = -> Part__Mirroring [Face7]
FEATURE [Sketcher::SketchObject] Sketch142
  ExternalGeometry = -> [Pad049]
  FullyConstrained = true
  MapMode = 5
  Placement = pos=(-15,3.7e-15,0) rot=(0.57735,0.57735,0.57735;2.0944rad)
  Support = -> [Pad049]
  sketch-geometry (4):
    g0: LineSegment StartX=-6.0324 StartY=-8.4676 StartZ=0 EndX=-15.1 EndY=-8.4676 EndZ=0
    g1: LineSegment StartX=-15.1 StartY=-8.4676 StartZ=0 EndX=-15.1 EndY=-0.6 EndZ=0
    g2: ArcOfCircle CenterX=-14.5 CenterY=-0.6 CenterZ=0 NormalX=0 NormalY=0 NormalZ=1 AngleXU=0 Radius=0.6 StartAngle=2e-16 EndAngle=3.14159
    g3: ArcOfCircle CenterX=-6.0324 CenterY=-0.6 CenterZ=0 NormalX=0 NormalY=0 NormalZ=1 AngleXU=0 Radius=7.8676 StartAngle=3.14159 EndAngle=4.71239
  constraints (10):
    c: Coincident(g0,g-3)
    c: Horizontal(g0)
    c: Coincident(g0,g1)
    c: PointOnObject(g1,g-3)
    c: Tangent(g3,g0) = 1.5708
    c: Tangent(g2,g1) = 1.5708
    c: Tangent(g3,g2) = 1.5708
    c: Diameter(g2) = 1.2
    c: Tangent(g-5,g2)
    c: Horizontal(g2,g1)
FEATURE [PartDesign::Pad] Pad053
  BaseFeature = -> Pad049
  Direction = (1,-0.3,0)
  Length = 10
  Length2 = 10
  Profile = -> Sketch142
  ReferenceAxis = -> Sketch142 [N_Axis]
  Type = 3
  UpToFace = -> Pad049 [Face11]
  UseCustomVector = true
FEATURE [PartDesign::Body] Body018  label="左"
  Group = -> [Sketch128,Pad047,Sketch129,Pocket065,Thickness,Sketch130,Pocket066,Sketch131,Pocket067,Sketch132,Pad048,Fillet,Chamfer,Chamfer001,Fillet001,Sketch133,Pocket068,Sketch134,Pad049,Sketch142,Pad053]
  Origin = -> Origin023
  Placement = pos=(-1.6,0,0) rot=(0,0,1;0rad)
  Tip = -> Pad053
FEATURE [Part::Fuse] Fusion  label="合并风道"
  Base = -> Body018
  Tool = -> Part__Mirroring
FEATURE [Part::Fuse] Fusion001  label="合并上下"
  Base = -> Body016
  Placement = pos=(35,0,-51.35) rot=(0,0,1;0rad)
  Tool = -> Fusion
